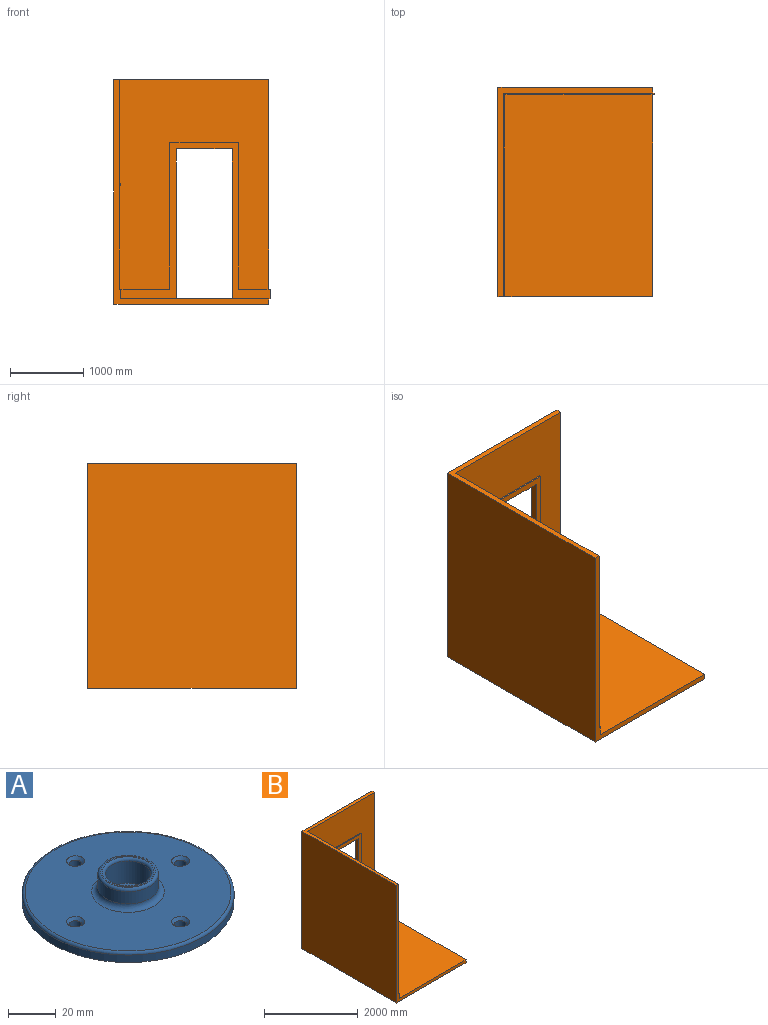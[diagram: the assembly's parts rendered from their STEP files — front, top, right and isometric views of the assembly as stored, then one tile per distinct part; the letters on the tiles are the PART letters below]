
ASSEMBLY  parts=2 mates=1
PART A: 19 faces, bbox 96.2x96.2x15.2 mm
  f0: cylinder r=44.45mm len=88.9mm, axis (0,0,-1), area 1064.1mm2, adj f2,f11
  f1: plane 86.36x86.36mm, normal (0,0,1), area 4945.5mm2, adj f11,f14,f15,f16,f17,f18
  f2: plane 88.9x88.9mm, normal (0,0,-1), area 6126.1mm2, adj f0,f7,f8,f9,f10
  f3: cylinder r=12.7mm len=25.4mm, axis (0,0,-1), area 506.7mm2, adj f12,f14
  f4: plane 22.86x22.86mm, normal (0,0,1), area 44.3mm2, adj f12,f13
  f5: cylinder r=9.53mm len=19.05mm, axis (0,0,1), area 684.1mm2, adj f6,f13
  f6: plane 19.05x19.05mm, normal (0,0,1), area 285mm2, adj f5
  f7: cylinder r=2.54mm len=5.08mm, axis (0,0,1), area 60.8mm2, adj f2,f16
  f8: cylinder r=2.54mm len=5.08mm, axis (0,0,1), area 60.8mm2, adj f2,f17
  f9: cylinder r=2.54mm len=5.08mm, axis (0,0,1), area 60.8mm2, adj f2,f18
  f10: cylinder r=2.54mm len=5.08mm, axis (0,0,1), area 60.8mm2, adj f2,f15
  f11: torus R=43.18mm, axis (0,0,1), area 551.4mm2, adj f0,f1
  f12: torus R=11.43mm, axis (0,0,1), area 153.4mm2, adj f3,f4
  f13: torus R=10.79mm, axis (0,0,1), area 125.2mm2, adj f4,f5
  f14: torus R=15.24mm, axis (0,0,1), area 341.5mm2, adj f1,f3
  f15: cone r=2.54mm half-angle=45deg, axis (0,0,1), area 35.8mm2, adj f1,f10
  f16: cone r=2.54mm half-angle=45deg, axis (0,0,1), area 35.8mm2, adj f1,f7
  f17: cone r=2.54mm half-angle=45deg, axis (0,0,1), area 35.8mm2, adj f1,f8
  f18: cone r=2.54mm half-angle=45deg, axis (0,0,1), area 35.8mm2, adj f1,f9
PART B: 22 faces, bbox 2127.3x2844.8x3067.1 mm
  f0: plane 2768.6x685.8mm, normal (0,0,1), area 65443.4mm2, adj f1,f2,f4,f6,f17,f20
  f1: plane 2857.5x2032mm, normal (0,-1,0), area 3926605.1mm2, adj f0,f3,f6,f7,f14,f19,f20,f21
  f2: plane 2749.55x133.35mm, normal (1,0,0), area 366652.5mm2, adj f0,f4,f9,f17
  f3: plane 2844.8x2108.2mm, normal (0,0,1), area 371612.2mm2, adj f1,f4,f5,f6,f7,f8
  f4: plane 3067.05x2108.2mm, normal (0,-1,0), area 391087.9mm2, adj f0,f2,f3,f5,f6,f7,f9,f10
  f5: plane 3067.05x2844.8mm, normal (-1,0,0), area 8725143.8mm2, adj f3,f4,f8,f10
  f6: plane 2857.5x2768.6mm, normal (1,0,0), area 7911274.5mm2, adj f0,f1,f3,f4
  f7: plane 3067.05x2844.8mm, normal (1,0,0), area 444676.5mm2, adj f1,f3,f4,f8,f9,f10,f15,f16
  f8: plane 3067.05x2108.2mm, normal (0,1,0), area 4907893.4mm2, adj f3,f5,f7,f9,f10,f11,f12,f13
  f9: plane 2844.8x2012.95mm, normal (0,0,1), area 5607287.2mm2, adj f2,f4,f7,f8,f11,f13,f17
  f10: plane 2844.8x2108.2mm, normal (0,0,-1), area 5997407.4mm2, adj f4,f5,f7,f8
  f11: plane 2044.7x95.25mm, normal (-1,0,0), area 194757.7mm2, adj f8,f9,f12,f17
  f12: plane 762x95.25mm, normal (0,0,-1), area 72580.5mm2, adj f8,f11,f13,f17
  f13: plane 2044.7x95.25mm, normal (1,0,0), area 194757.7mm2, adj f8,f9,f12,f17
  f14: plane 425.45x19.05mm, normal (0,0,1), area 8104.8mm2, adj f1,f15,f17,f18,f19
  f15: plane 133.35x19.05mm, normal (0,1,0), area 2540.3mm2, adj f7,f14,f16,f18
  f16: plane 19.05x19.05mm, normal (0,0,-1), area 362.9mm2, adj f7,f15,f17,f18
  f17: plane 2133.6x2032mm, normal (0,-1,0), area 592740.7mm2, adj f0,f2,f9,f11,f12,f13,f14,f16
  f18: plane 133.35x19.05mm, normal (1,0,0), area 2540.3mm2, adj f14,f15,f16,f17
  f19: plane 2000.25x19.05mm, normal (1,0,0), area 38104.8mm2, adj f1,f14,f17,f21
  f20: plane 2000.25x19.05mm, normal (-1,0,0), area 38104.8mm2, adj f0,f1,f17,f21
  f21: plane 939.8x19.05mm, normal (0,0,1), area 17903.2mm2, adj f1,f17,f19,f20
PLACE A rot(axis=(0.71,0,0.71),180deg) t=(-2936.13,-1147.57,128.19)mm
PLACE B t=(-2936.13,236.73,-1433.91)mm fixed
MATE fastened A.f0 <-> B.f6  axis (-1,0,0) through (-2936.13,-1147.57,128.19)mm
